# Revit family: Sanitary_Showers_hansgrohe_71408000-Logis-E-Single-lever-bath-mixer_
name_source: partatom
category: Plumbing Fixtures
revit_build: Autodesk Revit 2015 (Build: 20140903_1530(x64)
units: mm (PartAtom-declared; Revit-internal decimal feet)

## types (1)
- Chrome 000
    BIMobject category = Showers
    BIMobject category code = sanitary-showers
    BIMobject main category = Sanitary
    BIMobject main category code = sanitary
    Brand url = http://www.hansgrohe-int.com
    Default Elevation = 1219.2 mm  [stored 4 ft]
    Design country = Germany
    Edition number = 1
    GTIN code = https://4059625143346
    IFC Classification = Sanitary Terminal
    Manufacturer country = Germany
    Manufacturer name = hansgrohe
    Material main = Chrome
    Product Guid = eb5d2cf3-3c37-4c7c-bc78-b28730d9e9ac
    Product SKU = 71408000
    Product data url = https://bimobject.com
    Product family = Logis E
    Product group = Bath mixers
    Product name = 71408000 Logis E Single lever bath mixer set for concealed installation
    QR code = http://bimobject.com

note: [stored X ft] marks values corroborated as IEEE doubles in the binary element streams (Revit-internal decimal feet)

## geometry (parser evidence)
native form markers: Sweep x3
no freeform markers — native parametric forms only
